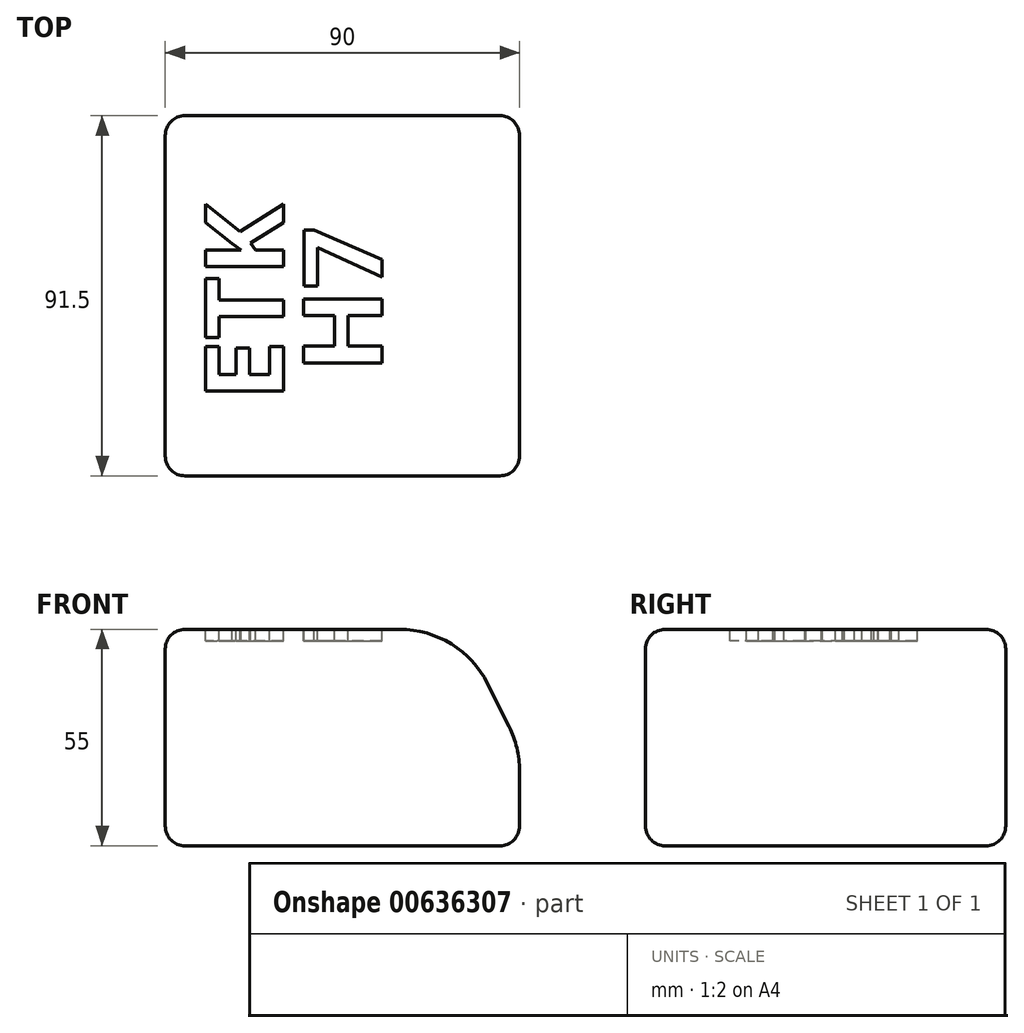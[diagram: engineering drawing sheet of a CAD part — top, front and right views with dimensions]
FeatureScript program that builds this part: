
annotation { "Feature Type Name" : "Feature", "Feature Type Description" : "" }
export const myFeature = defineFeature(function(context is Context, id is Id, definition is map)
    precondition{}
    {
        {
            var Q0;
            Q0=qCreatedBy(makeId("Front.planeOp"),FACE);
            var sketch = newSketch(context, id + "F0", { "sketchPlane" : qUnion([Q0])});
            skLineSegment(sketch, "E0", {"start": v(0, 0) * mm, "end": v(90, 0) * mm});
            skLineSegment(sketch, "E1", {"start": v(90, 0) * mm, "end": v(90, 19.1) * mm});
            skLineSegment(sketch, "E2", {"start": v(87.36, 30.28) * mm, "end": v(81.9, 41.18) * mm});
            skLineSegment(sketch, "E3", {"start": v(59.55, 55) * mm, "end": v(0, 55) * mm});
            skLineSegment(sketch, "E4", {"start": v(0, 55) * mm, "end": v(0, 0) * mm});
            skPoint(sketch, "E5.visualSharp", {"position": v(75, 55) * mm});
            skArc(sketch, "E5.filletArc", {"start": v(81.9, 41.18) * mm, "mid": v(72.7, 51.27) * mm, "end": v(59.55, 55) * mm});
            skPoint(sketch, "E6.visualSharp", {"position": v(90, 25) * mm});
            skArc(sketch, "E6.filletArc", {"start": v(90, 19.1) * mm, "mid": v(89.33, 24.84) * mm, "end": v(87.36, 30.28) * mm});
            skSolve(sketch);
        }
        {
            var Q0;
            Q0=qSketchRegion(id+"F0",true);
            extrude(context, id + "F1", {"entities" : qUnion([Q0]), "depth" : 91.5 * mm, "offsetDistance" : 25 * mm});
        }
        {
            var Q0;
            Q0=makeQuery(id+"F1.opExtrude","CAP_EDGE",EDGE,{"disambiguationData":[OSD([sQuery(id+"F0.wireOp",EDGE,"E3")])],"isStart":false});
            var Q1;
            Q1=makeQuery(id+"F1.opExtrude","CAP_EDGE",EDGE,{"disambiguationData":[OSD([sQuery(id+"F0.wireOp",EDGE,"E4")])],"isStart":false});
            var Q2;
            Q2=makeQuery(id+"F1.opExtrude","CAP_EDGE",EDGE,{"disambiguationData":[OSD([sQuery(id+"F0.wireOp",EDGE,"E0")])],"isStart":false});
            var Q3;
            Q3=makeQuery(id+"F1.opExtrude","CAP_EDGE",EDGE,{"disambiguationData":[OSD([sQuery(id+"F0.wireOp",EDGE,"E3")])],"isStart":true});
            var Q4;
            Q4=makeQuery(id+"F1.opExtrude","CAP_EDGE",EDGE,{"disambiguationData":[OSD([sQuery(id+"F0.wireOp",EDGE,"E0")])],"isStart":true});
            var Q5;
            Q5=makeQuery(id+"F1.opExtrude","CAP_EDGE",EDGE,{"disambiguationData":[OSD([sQuery(id+"F0.wireOp",EDGE,"E4")])],"isStart":true});
            var Q6;
            Q6=makeQuery(id+"F1.opExtrude","SWEPT_EDGE",EDGE,{"disambiguationData":[OSD([sQuery(id+"F0.wireOp",EDGE,"E0"),sQuery(id+"F0.wireOp",EDGE,"E4")])]});
            var Q7;
            Q7=makeQuery(id+"F1.opExtrude","SWEPT_EDGE",EDGE,{"disambiguationData":[OSD([sQuery(id+"F0.wireOp",EDGE,"E3"),sQuery(id+"F0.wireOp",EDGE,"E4")])]});
            var Q8;
            Q8=makeQuery(id+"F1.opExtrude","SWEPT_EDGE",EDGE,{"disambiguationData":[OSD([sQuery(id+"F0.wireOp",EDGE,"E0"),sQuery(id+"F0.wireOp",EDGE,"E1")])]});
            fillet(context, id + "F2", {"entities" : qUnion([Q0, Q1, Q2, Q3, Q4, Q5, Q6, Q7, Q8]), "radius" : 5 * mm, "tangentPropagation" : true, "allowEdgeOverflow" : false});
        }
        {
            var Q0;
            Q0=makeQuery(id+"F1.opExtrude","SWEPT_FACE",FACE,{"disambiguationData":[OSD([sQuery(id+"F0.wireOp",EDGE,"E3")])]});
            var sketch = newSketch(context, id + "F3", { "sketchPlane" : qUnion([Q0])});
            skText(sketch, "E7", { "text": "ETK", "fontName": "OpenSans-Bold.ttf"});
            const initialGuessF3  = {"E7": [0.03, -0.0725, 0, 1, 0.02]};
            skSetInitialGuess(sketch, initialGuessF3);
            skSolve(sketch);
        }
        {
            var Q0;
            Q0=makeQuery(id+"F1.opExtrude","SWEPT_FACE",FACE,{"disambiguationData":[OSD([sQuery(id+"F0.wireOp",EDGE,"E3")])]});
            var sketch = newSketch(context, id + "F4", { "sketchPlane" : qUnion([Q0])});
            skText(sketch, "E8", { "text": " H7", "fontName": "OpenSans-Bold.ttf"});
            const initialGuessF4  = {"E8": [0.055, -0.0725, 0, 1, 0.02]};
            skSetInitialGuess(sketch, initialGuessF4);
            skSolve(sketch);
        }
        {
            var Q0;
            Q0=qSketchRegion(id+"F3",true);
            var Q1;
            Q1=qSketchRegion(id+"F4",true);
            extrude(context, id + "F5", {"entities" : qUnion([Q0, Q1]), "operationType" : NewBodyOperationType.REMOVE, "surfaceOperationType" : NewSurfaceOperationType.ADD, "oppositeDirection" : true, "depth" : 3 * mm, "offsetDistance" : 25 * mm});
        }
    });
